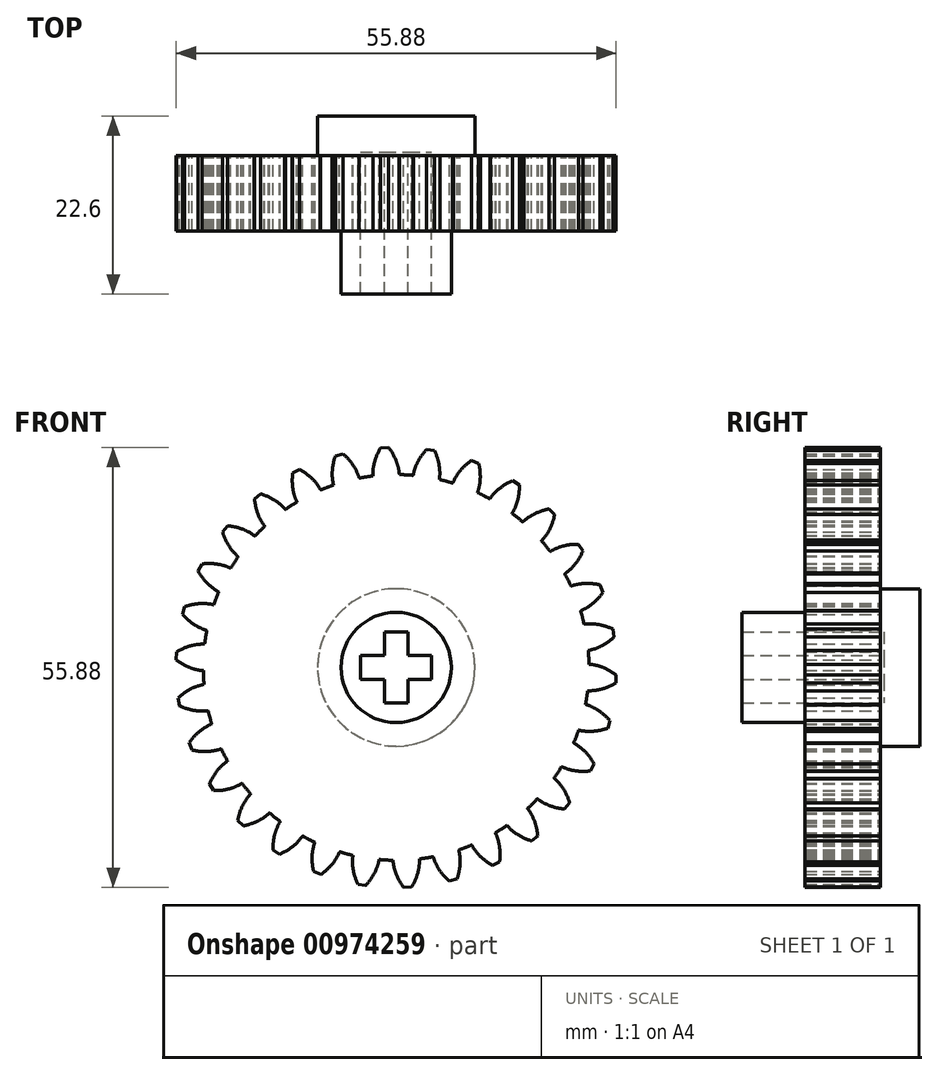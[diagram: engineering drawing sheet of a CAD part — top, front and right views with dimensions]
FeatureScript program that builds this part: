
annotation { "Feature Type Name" : "Feature", "Feature Type Description" : "" }
export const myFeature = defineFeature(function(context is Context, id is Id, definition is map)
    precondition{}
    {
        {
            var Q0;
            Q0=qCreatedBy(makeId("Front.planeOp"),FACE);
            var sketch = newSketch(context, id + "F0", { "sketchPlane" : qUnion([Q0])});
            skCircle(sketch, "E0", {"center": v(0, 0) * mm, "radius": 24.5 * mm});
            skCircle(sketch, "E1", {"center": v(0, 0) * mm, "radius": 26.25 * mm, "construction": true});
            skLineSegment(sketch, "E2", {"start": v(0, 0) * mm, "end": v(0, 39.24) * mm, "construction": true});
            skLineSegment(sketch, "E3", {"start": v(0, 0) * mm, "end": v(-2.1, 40.22) * mm, "construction": true});
            skCircle(sketch, "E4", {"center": v(0, 26.25) * mm, "radius": 6.57 * mm, "construction": true});
            skLineSegment(sketch, "E5", {"start": v(0, 26.25) * mm, "end": v(-16.36, 26.25) * mm, "construction": true});
            skLineSegment(sketch, "E6", {"start": v(0, 26.25) * mm, "end": v(-16.51, 20.24) * mm, "construction": true});
            skCircle(sketch, "E7", {"center": v(0, 0) * mm, "radius": 24.67 * mm, "construction": true});
            skCircle(sketch, "E8", {"center": v(-6.13, 23.9) * mm, "radius": 6.57 * mm, "construction": true});
            skArc(sketch, "E9", {"start": v(0.4, 24.67) * mm, "mid": v(0.25, 25.47) * mm, "end": v(0, 26.25) * mm});
            skArc(sketch, "E10", {"start": v(0.4, 24.67) * mm, "mid": v(0.4, 24.58) * mm, "end": v(0.4, 24.5) * mm});
            skArc(sketch, "E11.MirrorCS", {"start": v(-2.97, 24.5) * mm, "mid": v(-2.9, 25.3) * mm, "end": v(-2.74, 26.1) * mm});
            skArc(sketch, "E12.MirrorCS", {"start": v(-2.97, 24.5) * mm, "mid": v(-2.96, 24.4) * mm, "end": v(-2.97, 24.32) * mm});
            skCircle(sketch, "E13", {"center": v(0, 0) * mm, "radius": 28 * mm, "construction": true});
            skArc(sketch, "E14", {"start": v(0, 26.25) * mm, "mid": v(-0.42, 27.13) * mm, "end": v(-0.96, 27.94) * mm});
            skArc(sketch, "E15.MirrorCS", {"start": v(-2.74, 26.1) * mm, "mid": v(-2.42, 27.03) * mm, "end": v(-1.97, 27.9) * mm});
            skLineSegment(sketch, "E16", {"start": v(-1.97, 27.9) * mm, "end": v(-0.96, 27.94) * mm});
            skSolve(sketch);
        }
        {
            var Q0;
            Q0=makeQuery(id+"F0.imprint","IMPRINT",FACE,{"disambiguationData":[TD([[makeQuery(id+"F0.imprint","IMPRINT",EDGE,{"derivedFrom":sQuery(id+"F0.wireOp",EDGE,"xuahpPEx-bPpa-uA6E-2FwE-3edqL7deXWHO")}),1.0]])]});
            var Q1;
            {var subQ0=sQuery(id+"F0.wireOp",EDGE,"E0");var subQ1=makeQuery(id+"F0.imprint","INTERSECT",VERTEX,{"derivedFrom":[subQ0,sQuery(id+"F0.wireOp",EDGE,"E10")]});Q1=makeQuery(id+"F0.imprint","IMPRINT",FACE,{"disambiguationData":[TD([[makeQuery(id+"F0.imprint","IMPRINT",EDGE,{"disambiguationData":[TD([[subQ1,-1.0]])],"derivedFrom":subQ0}),1.0]])]});}
            var Q2;
            Q2=makeQuery(id+"F0.imprint","IMPRINT",FACE,{"disambiguationData":[TD([[makeQuery(id+"F0.imprint","IMPRINT",EDGE,{"derivedFrom":sQuery(id+"F0.wireOp",EDGE,"E9")}),1.0]])]});
            extrude(context, id + "F1", {"entities" : qUnion([Q0, Q1, Q2]), "depth" : 9.6 * mm, "offsetDistance" : 25 * mm});
        }
        {
            var Q0;
            Q0=makeQuery(id+"F1.opExtrude","SWEPT_BODY",BODY,{"disambiguationData":[OSD([sQuery(id+"F0.wireOp",EDGE,"E0"),sQuery(id+"F0.wireOp",EDGE,"xuahpPEx-bPpa-uA6E-2FwE-3edqL7deXWHO"),sQuery(id+"F0.wireOp",EDGE,"E9"),sQuery(id+"F0.wireOp",EDGE,"E10"),sQuery(id+"F0.wireOp",EDGE,"fba4ba2b-13ca-409a-a92f-8408ce5fe5520.MirrorCS"),sQuery(id+"F0.wireOp",EDGE,"E11.MirrorCS"),sQuery(id+"F0.wireOp",EDGE,"E12.MirrorCS")])]});
            var Q1;
            Q1=makeQuery(id+"F1.opExtrude","CAP_EDGE",EDGE,{"disambiguationData":[OSD([sQuery(id+"F0.wireOp",EDGE,"E0")])],"isStart":true});
            circularPattern(context, id + "F2", {"entities" : qUnion([Q0]), "axis" : qUnion([Q1]), "angle" : 360 * degree, "instanceCount" : 30, "equalSpace" : true});
        }
        {
            var Q0;
            Q0=makeQuery(id+"F2.opPattern","COPY",FACE,{"derivedFrom":makeQuery(id+"F1.opExtrude","CAP_FACE",FACE,{"disambiguationData":[OSD([sQuery(id+"F0.wireOp",EDGE,"E0"),sQuery(id+"F0.wireOp",EDGE,"xuahpPEx-bPpa-uA6E-2FwE-3edqL7deXWHO"),sQuery(id+"F0.wireOp",EDGE,"E9"),sQuery(id+"F0.wireOp",EDGE,"E10"),sQuery(id+"F0.wireOp",EDGE,"fba4ba2b-13ca-409a-a92f-8408ce5fe5520.MirrorCS"),sQuery(id+"F0.wireOp",EDGE,"E11.MirrorCS"),sQuery(id+"F0.wireOp",EDGE,"E12.MirrorCS")])],"isStart":true}),"instanceName":"1"});
            var sketch = newSketch(context, id + "F3", { "sketchPlane" : qUnion([Q0])});
            skCircle(sketch, "E17", {"center": v(0, 0) * mm, "radius": 10 * mm});
            skSolve(sketch);
        }
        {
            var Q0;
            Q0=makeQuery(id+"F3.imprint","IMPRINT",FACE,{"disambiguationData":[TD([[makeQuery(id+"F3.imprint","IMPRINT",EDGE,{"derivedFrom":sQuery(id+"F3.wireOp",EDGE,"E17")}),1.0]])]});
            extrude(context, id + "F4", {"entities" : qUnion([Q0]), "operationType" : NewBodyOperationType.ADD, "depth" : 5 * mm, "offsetDistance" : 25 * mm});
        }
        {
            var Q0;
            {var subQ0=makeQuery(id+"F1.opExtrude","CAP_FACE",FACE,{"disambiguationData":[OSD([sQuery(id+"F0.wireOp",EDGE,"E0"),sQuery(id+"F0.wireOp",EDGE,"xuahpPEx-bPpa-uA6E-2FwE-3edqL7deXWHO"),sQuery(id+"F0.wireOp",EDGE,"E9"),sQuery(id+"F0.wireOp",EDGE,"E10"),sQuery(id+"F0.wireOp",EDGE,"fba4ba2b-13ca-409a-a92f-8408ce5fe5520.MirrorCS"),sQuery(id+"F0.wireOp",EDGE,"E11.MirrorCS"),sQuery(id+"F0.wireOp",EDGE,"E12.MirrorCS")])],"isStart":false});Q0=makeQuery(id+"F4.boolean.opBoolean","MERGE",FACE,{"derivedFrom":[subQ0,makeQuery(id+"F2.opPattern","COPY",FACE,{"derivedFrom":subQ0,"instanceName":"1"}),makeQuery(id+"F2.opPattern","COPY",FACE,{"derivedFrom":subQ0,"instanceName":"2"}),makeQuery(id+"F2.opPattern","COPY",FACE,{"derivedFrom":subQ0,"instanceName":"3"}),makeQuery(id+"F2.opPattern","COPY",FACE,{"derivedFrom":subQ0,"instanceName":"4"}),makeQuery(id+"F2.opPattern","COPY",FACE,{"derivedFrom":subQ0,"instanceName":"5"}),makeQuery(id+"F2.opPattern","COPY",FACE,{"derivedFrom":subQ0,"instanceName":"6"}),makeQuery(id+"F2.opPattern","COPY",FACE,{"derivedFrom":subQ0,"instanceName":"7"}),makeQuery(id+"F2.opPattern","COPY",FACE,{"derivedFrom":subQ0,"instanceName":"8"}),makeQuery(id+"F2.opPattern","COPY",FACE,{"derivedFrom":subQ0,"instanceName":"9"}),makeQuery(id+"F2.opPattern","COPY",FACE,{"derivedFrom":subQ0,"instanceName":"10"}),makeQuery(id+"F2.opPattern","COPY",FACE,{"derivedFrom":subQ0,"instanceName":"11"}),makeQuery(id+"F2.opPattern","COPY",FACE,{"derivedFrom":subQ0,"instanceName":"12"}),makeQuery(id+"F2.opPattern","COPY",FACE,{"derivedFrom":subQ0,"instanceName":"13"}),makeQuery(id+"F2.opPattern","COPY",FACE,{"derivedFrom":subQ0,"instanceName":"14"}),makeQuery(id+"F2.opPattern","COPY",FACE,{"derivedFrom":subQ0,"instanceName":"15"}),makeQuery(id+"F2.opPattern","COPY",FACE,{"derivedFrom":subQ0,"instanceName":"16"}),makeQuery(id+"F2.opPattern","COPY",FACE,{"derivedFrom":subQ0,"instanceName":"17"}),makeQuery(id+"F2.opPattern","COPY",FACE,{"derivedFrom":subQ0,"instanceName":"18"}),makeQuery(id+"F2.opPattern","COPY",FACE,{"derivedFrom":subQ0,"instanceName":"19"}),makeQuery(id+"F2.opPattern","COPY",FACE,{"derivedFrom":subQ0,"instanceName":"20"}),makeQuery(id+"F2.opPattern","COPY",FACE,{"derivedFrom":subQ0,"instanceName":"21"}),makeQuery(id+"F2.opPattern","COPY",FACE,{"derivedFrom":subQ0,"instanceName":"22"}),makeQuery(id+"F2.opPattern","COPY",FACE,{"derivedFrom":subQ0,"instanceName":"23"}),makeQuery(id+"F2.opPattern","COPY",FACE,{"derivedFrom":subQ0,"instanceName":"24"}),makeQuery(id+"F2.opPattern","COPY",FACE,{"derivedFrom":subQ0,"instanceName":"25"}),makeQuery(id+"F2.opPattern","COPY",FACE,{"derivedFrom":subQ0,"instanceName":"26"}),makeQuery(id+"F2.opPattern","COPY",FACE,{"derivedFrom":subQ0,"instanceName":"27"}),makeQuery(id+"F2.opPattern","COPY",FACE,{"derivedFrom":subQ0,"instanceName":"28"}),makeQuery(id+"F2.opPattern","COPY",FACE,{"derivedFrom":subQ0,"instanceName":"29"})]});}
            var sketch = newSketch(context, id + "F5", { "sketchPlane" : qUnion([Q0])});
            skCircle(sketch, "E18", {"center": v(0, 0) * mm, "radius": 7 * mm});
            skLineSegment(sketch, "E19", {"start": v(-4.5, 1.5) * mm, "end": v(4.5, 1.5) * mm});
            skLineSegment(sketch, "E20.MirrorCS", {"start": v(-4.5, -1.5) * mm, "end": v(4.5, -1.5) * mm});
            skLineSegment(sketch, "E21", {"start": v(-1.5, 4.5) * mm, "end": v(-1.5, -4.5) * mm});
            skLineSegment(sketch, "E22.MirrorCS", {"start": v(1.5, 4.5) * mm, "end": v(1.5, -4.5) * mm});
            skLineSegment(sketch, "E23", {"start": v(-1.5, 4.5) * mm, "end": v(1.5, 4.5) * mm});
            skLineSegment(sketch, "E24", {"start": v(-4.5, 1.5) * mm, "end": v(-4.5, -1.5) * mm});
            skLineSegment(sketch, "E25.MirrorCS", {"start": v(-1.5, -4.5) * mm, "end": v(1.5, -4.5) * mm});
            skLineSegment(sketch, "E26.MirrorCS", {"start": v(4.5, 1.5) * mm, "end": v(4.5, -1.5) * mm});
            skSolve(sketch);
        }
        {
            var Q0;
            Q0=makeQuery(id+"F5.imprint","IMPRINT",FACE,{"disambiguationData":[TD([[makeQuery(id+"F5.imprint","IMPRINT",EDGE,{"derivedFrom":sQuery(id+"F5.wireOp",EDGE,"E18")}),1.0]])]});
            var Q1;
            Q1=sQuery(id+"F5.wireOp",EDGE,"E18");
            extrude(context, id + "F6", {"entities" : qUnion([Q0]), "operationType" : NewBodyOperationType.ADD, "surfaceOperationType" : NewSurfaceOperationType.ADD, "surfaceEntities" : qUnion([Q1]), "depth" : 8 * mm, "offsetDistance" : 25 * mm});
        }
        {
            var Q0;
            {var subQ0=sQuery(id+"F5.wireOp",EDGE,"E24");Q0=makeQuery(id+"F5.imprint","IMPRINT",FACE,{"disambiguationData":[TD([[makeQuery(id+"F5.imprint","IMPRINT",EDGE,{"derivedFrom":subQ0}),1.0]])]});}
            var Q1;
            {var subQ5=sQuery(id+"F5.wireOp",EDGE,"E23");Q1=makeQuery(id+"F5.imprint","IMPRINT",FACE,{"disambiguationData":[TD([[makeQuery(id+"F5.imprint","IMPRINT",EDGE,{"derivedFrom":subQ5}),-1.0]])]});}
            var Q2;
            {var subQ0=sQuery(id+"F5.wireOp",EDGE,"E26.MirrorCS");Q2=makeQuery(id+"F5.imprint","IMPRINT",FACE,{"disambiguationData":[TD([[makeQuery(id+"F5.imprint","IMPRINT",EDGE,{"derivedFrom":subQ0}),-1.0]])]});}
            var Q3;
            {var subQ0=sQuery(id+"F5.wireOp",EDGE,"E21");var subQ1=sQuery(id+"F5.wireOp",EDGE,"E19");var subQ2=makeQuery(id+"F5.imprint","INTERSECT",VERTEX,{"derivedFrom":[subQ1,subQ0]});Q3=makeQuery(id+"F5.imprint","IMPRINT",FACE,{"disambiguationData":[TD([[makeQuery(id+"F5.imprint","IMPRINT",EDGE,{"disambiguationData":[TD([[subQ2,-1.0]])],"derivedFrom":subQ1}),-1.0]])]});}
            var Q4;
            {var subQ5=sQuery(id+"F5.wireOp",EDGE,"E25.MirrorCS");Q4=makeQuery(id+"F5.imprint","IMPRINT",FACE,{"disambiguationData":[TD([[makeQuery(id+"F5.imprint","IMPRINT",EDGE,{"derivedFrom":subQ5}),1.0]])]});}
            extrude(context, id + "F7", {"entities" : qUnion([Q0, Q1, Q2, Q3, Q4]), "operationType" : NewBodyOperationType.REMOVE, "oppositeDirection" : true, "depth" : 10 * mm, "offsetDistance" : 25 * mm});
        }
    });
